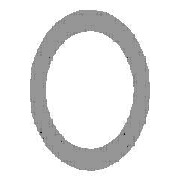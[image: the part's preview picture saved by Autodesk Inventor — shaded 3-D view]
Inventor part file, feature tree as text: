
AUTODESK INVENTOR PART (.ipt)
format: ipt  version: 2013 (Build 170138000, 138)  size: 125,952 bytes
history: native  units: mm (DEFAULTED — no unit token found)
features: plane x7, sketch x5, other x4, extrude x2
ambient origin geometry x8: Origin, YZ Plane, XZ Plane, XY Plane, X Axis, Y Axis, Z Axis, Center Point
bodies: Solid1 (feature_tree), Body (feature_tree)
feature tree (18):
  parser-record x1  (decoder bookkeeping rows leaked as tree rows — omitted from the tree; the rows remain in map.json)
  other  "Driven Length"
  other  "Start plane"
  other  "End plane"
  plane  "Work Plane4"
  plane  "Work Plane5"
  plane  "Work Plane6"
  extrude  "Extrusion2"  Depth=3.3782mm
  plane  "Work Plane7"
  plane  "Work Plane8"
  plane  "Work Plane9"
  extrude  "Extrusion3"  TaperAngle=0.0deg  [1 undecoded]
  sketch  "Sketch"  dims[d7=406.4mm d8=3.302mm d9=0.0mm d10=3.302mm d11=0.0mm]
  sketch  "Sketch3"  dims[d0=33.401mm d1=3.3782mm]
  plane  "Work Plane3"
  sketch  "Sketch4"  dims[d2=406.4mm d3=0.0mm d4=-0.0mm]
  sketch  "Sketch5"  dims[d5=406.4mm]
  sketch  "Sketch6"  dims[d6=90.0deg]
note: 1 required parameter value undecoded (feature->parameter linkage not recoverable at this tier; creation-order binding heuristic only, values carry confidence <= 0.55)
